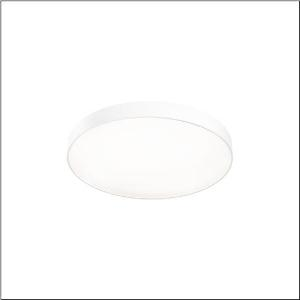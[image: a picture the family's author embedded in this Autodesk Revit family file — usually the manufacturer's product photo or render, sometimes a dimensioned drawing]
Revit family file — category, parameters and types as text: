
# Revit family: round_21_m_51mr36fm8321w
name_source: partatom
category: Lighting Fixtures
units: mm (PartAtom-declared; Revit-internal decimal feet)

## family parameters
Cut with Voids When Loaded = No
Host = Face
Light Source = No
Part Type = Normal
Room Calculation Point = No
Round Connector Dimension = Use Diameter
Shared = No

## types (1)
- --- (1 x LED, 8540 lm, 62.6 W, 3000K)
    Apparent Load = 63 VA
    CIE Flux Codes = 49 80 96 100 100
    Color Rendering = 80
    Color Temperature = 3000K
    Default Elevation = 1800 mm
    Description = Round 21 M, wall and ceiling luminaire, primary optical cover: cover, of PMMA, opal, light emission: direct distribution, primary light characteristic: symmetric, installation type: surface-mounted, suspended mounting, LED, rated luminous flux: 7.700lm, luminous efficacy: 127lm/W, light colour: 830, colour temperature: 3000K, control gear: ON/OFF Multilumen, with terminal, 3-pole, mains connection: 230V, AC, 50/60Hz, rated input power: 61W, housing, of aluminium, coated, white, diameter: 600mm, height: 62mm, protection rating (complete): IP40, insulation class (complete): insulation class I (protective earthing), certification: CE, impact resistance: IK04, permissible operating ambient temperature: -10..+35°C, packaging unit: 1 piece
    Height = 87 mm
    Lamp = 1 x LED
    Lamp Light Flux = 8540 lm
    Lamp Power = 62.6 W
    Lamp count = 1
    Length = 600 mm
    Luminous efficacy = 136 lm/W
    Manufacturer = Siteco
    ModVariant = No
    Model = 51MR36FM8321W
    Mounting Place = Ceiling
    Mounting Type = Surface mounted
    Number of Poles = 1
    OnlyDefault = Yes
    Power Factor = 1
    Product Name = Round 21 M
    Product group = wall and ceiling luminaire | ceiling mounted
    ProductGroupID = 304
    Protection Class = Protection class I
    Protection Degree = IP 40
    RLX_Detail_Level = 1
    RLX_Emergency_Light_Flux = 0 lm
    RLX_Emergency_Type = 0
    RLX_Emergency_Type_DB = No
    RlxData = <blob elided: 14385 chars, md5=d436b0f1>
    Socket = socket
    Standby Power = 0 W
    System Light Flux = 8540 lm
    System Power = 63 W
    Type Comments = factory setting: luminous flux: 100 % | (ON | ON | ON | ON) | 700 mA
    Type Image = l_1258330.jpg
    URL = http://relux.com
    VarID = @adj_041075
    Voltage = 0 V
    Weight = 0.00 kg
    Width = 0 mm  [stored 0 ft]

note: [stored X ft] marks values corroborated as IEEE doubles in the binary element streams (Revit-internal decimal feet)

## geometry (parser evidence)
native form markers: Sweep x12
no freeform markers — native parametric forms only
